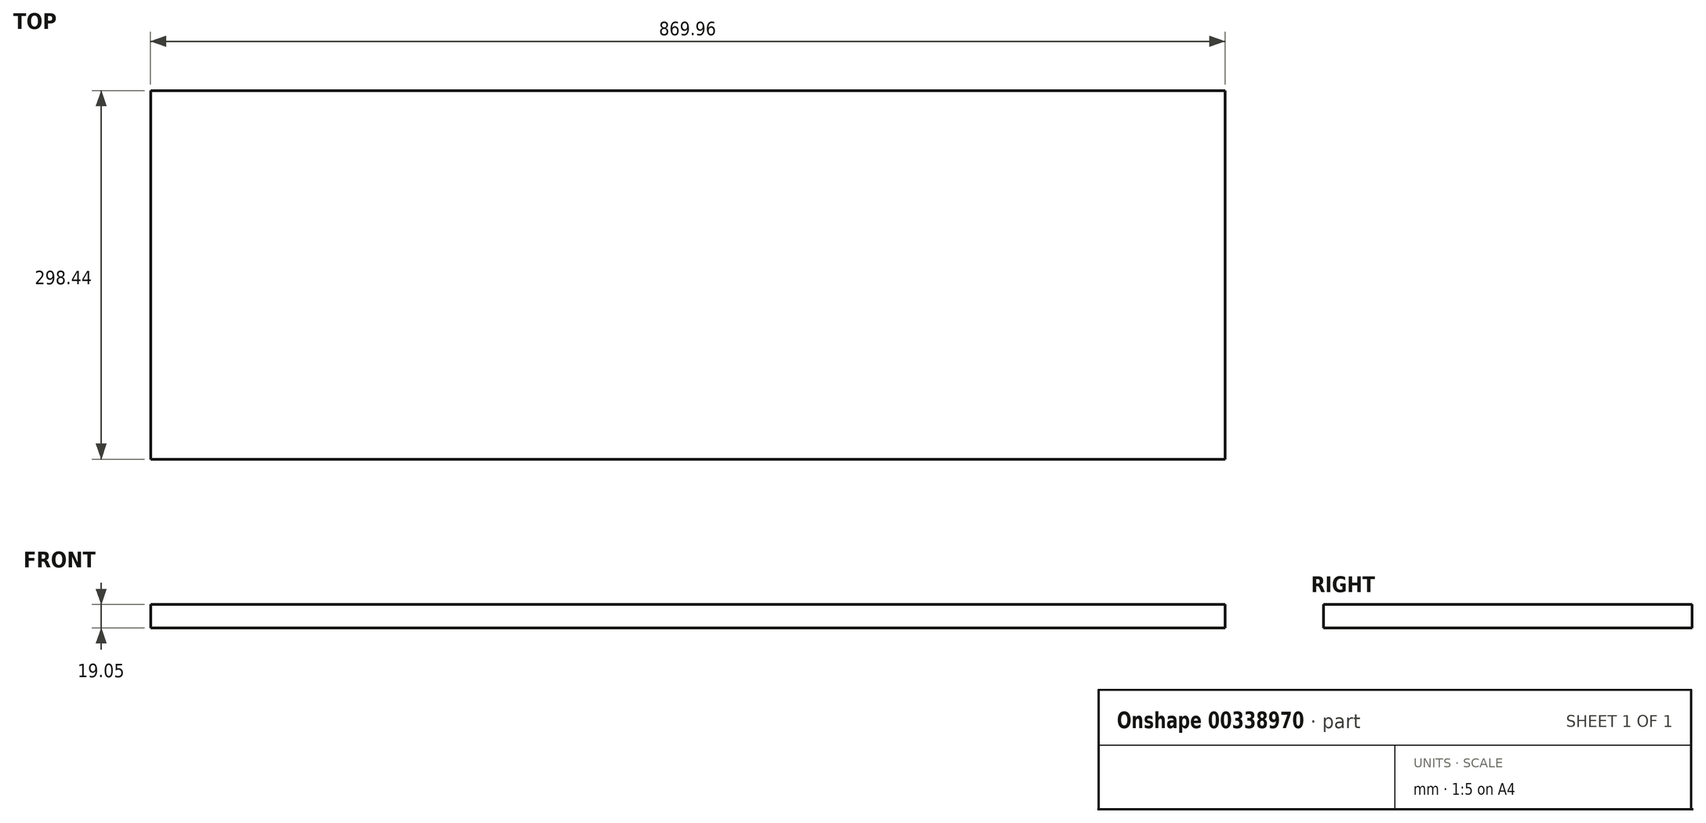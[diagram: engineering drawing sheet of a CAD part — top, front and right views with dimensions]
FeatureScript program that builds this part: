
annotation { "Feature Type Name" : "Feature", "Feature Type Description" : "" }
export const myFeature = defineFeature(function(context is Context, id is Id, definition is map)
    precondition{}
    {
        {
            var Q0;
            Q0=qCreatedBy(makeId("Top.planeOp"),FACE);
            var sketch = newSketch(context, id + "F0", { "sketchPlane" : qUnion([Q0])});
            skLineSegment(sketch, "E0.bottom", {"start": v(434.98, -149.22) * mm, "end": v(-434.98, -149.23) * mm});
            skLineSegment(sketch, "E0.top", {"start": v(434.98, 149.23) * mm, "end": v(-434.98, 149.22) * mm});
            skLineSegment(sketch, "E0.left", {"start": v(434.98, -149.22) * mm, "end": v(434.98, 149.23) * mm});
            skLineSegment(sketch, "E0.right", {"start": v(-434.98, -149.23) * mm, "end": v(-434.98, 149.22) * mm});
            skPoint(sketch, "E0.middle", {"position": v(0, 0) * mm});
            skSolve(sketch);
        }
        {
            var Q0;
            Q0 = qSketchRegion(id + "F0", true);
            extrude(context, id + "F1", {"entities" : qUnion([Q0]), "depth" : 19.05 * mm});
        }
    });
